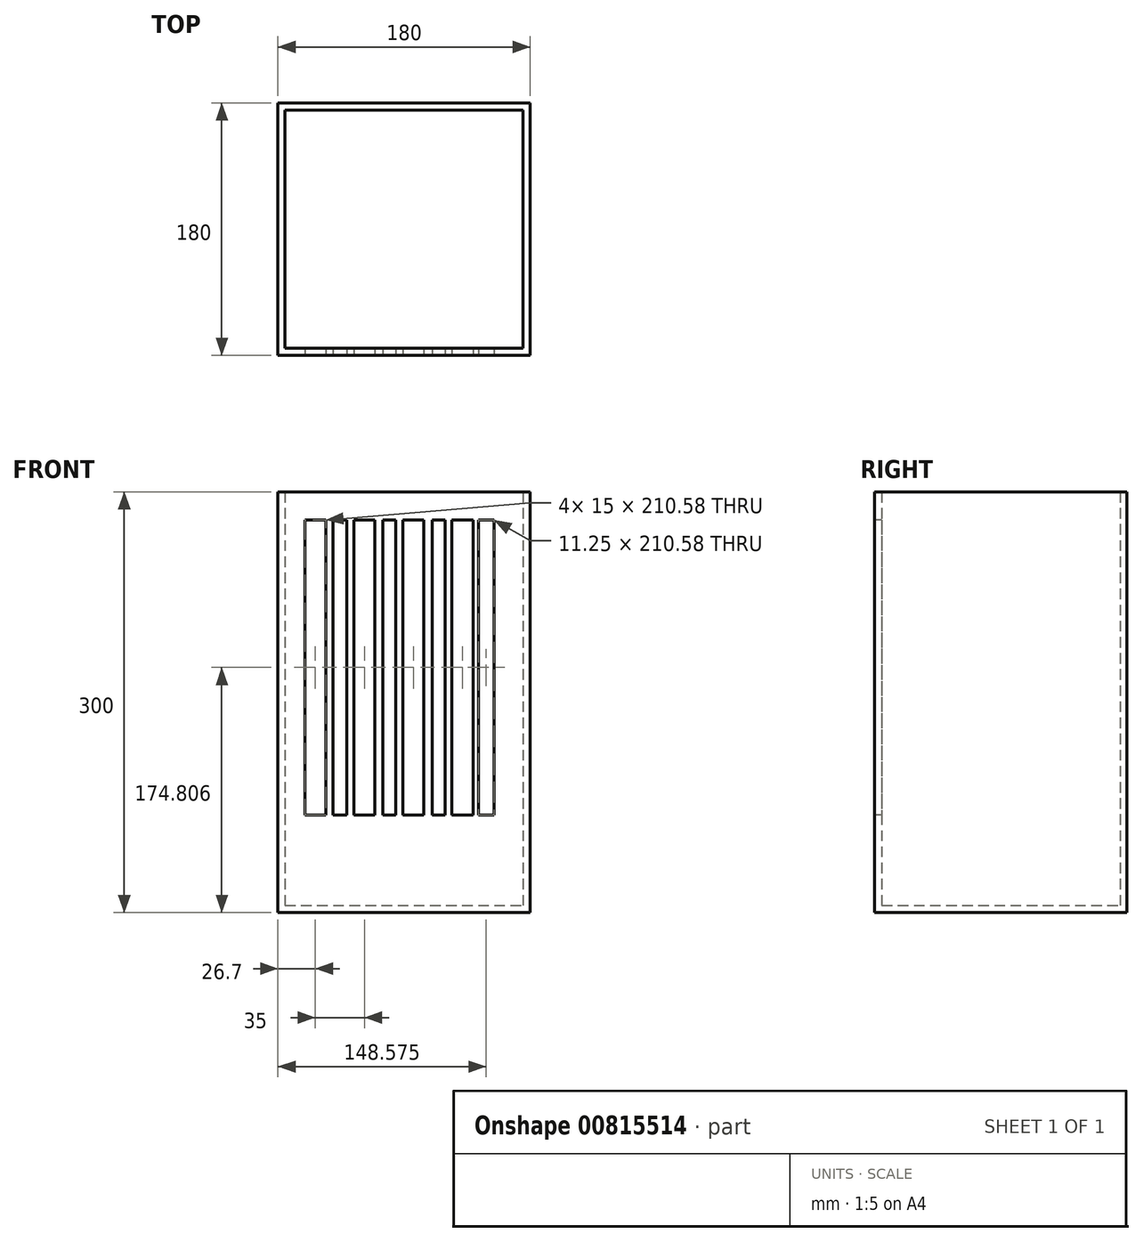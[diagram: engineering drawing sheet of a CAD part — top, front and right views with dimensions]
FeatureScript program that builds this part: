
annotation { "Feature Type Name" : "Feature", "Feature Type Description" : "" }
export const myFeature = defineFeature(function(context is Context, id is Id, definition is map)
    precondition{}
    {
        {
            var Q0;
            Q0=qCreatedBy(makeId("Front.planeOp"),FACE);
            var sketch = newSketch(context, id + "F0", { "sketchPlane" : qUnion([Q0])});
            skLineSegment(sketch, "E0.bottom", {"start": v(-142.95, 147.84) * mm, "end": v(37.05, 147.84) * mm});
            skLineSegment(sketch, "E0.top", {"start": v(-142.95, -152.16) * mm, "end": v(37.05, -152.16) * mm});
            skLineSegment(sketch, "E0.left", {"start": v(-142.95, 147.84) * mm, "end": v(-142.95, -152.16) * mm});
            skLineSegment(sketch, "E0.right", {"start": v(37.05, 147.84) * mm, "end": v(37.05, -152.16) * mm});
            skSolve(sketch);
        }
        {
            var Q0;
            Q0=makeQuery(id+"F0.imprint","IMPRINT",FACE,{"disambiguationData":[TD([[makeQuery(id+"F0.imprint","IMPRINT",EDGE,{"derivedFrom":sQuery(id+"F0.wireOp",EDGE,"E0.bottom")}),-1.0]])]});
            extrude(context, id + "F1", {"entities" : qUnion([Q0]), "depth" : 180 * mm, "offsetDistance" : 25 * mm});
        }
        {
            var Q0;
            Q0=makeQuery(id+"F1.opExtrude","SWEPT_FACE",FACE,{"disambiguationData":[OSD([sQuery(id+"F0.wireOp",EDGE,"E0.bottom")])]});
            shell(context, id + "F2", {"entities" : qUnion([Q0]), "thickness" : 5 * mm});
        }
        {
            var Q0;
            Q0=makeQuery(id+"F1.opExtrude","CAP_FACE",FACE,{"disambiguationData":[OSD([sQuery(id+"F0.wireOp",EDGE,"E0.bottom"),sQuery(id+"F0.wireOp",EDGE,"E0.top"),sQuery(id+"F0.wireOp",EDGE,"E0.left"),sQuery(id+"F0.wireOp",EDGE,"E0.right")])],"isStart":false});
            var sketch = newSketch(context, id + "F3", { "sketchPlane" : qUnion([Q0])});
            skLineSegment(sketch, "E1.bottom", {"start": v(-123.75, 127.94) * mm, "end": v(-108.75, 127.94) * mm});
            skLineSegment(sketch, "E1.top", {"start": v(-123.75, -82.65) * mm, "end": v(-108.75, -82.65) * mm});
            skLineSegment(sketch, "E1.left", {"start": v(-123.75, 127.94) * mm, "end": v(-123.75, -82.65) * mm});
            skLineSegment(sketch, "E1.right", {"start": v(-93.75, 127.94) * mm, "end": v(-93.75, -82.65) * mm});
            skLineSegment(sketch, "E2.bottom", {"start": v(-88.75, 127.94) * mm, "end": v(-73.75, 127.94) * mm});
            skLineSegment(sketch, "E2.top", {"start": v(-88.75, -82.65) * mm, "end": v(-73.75, -82.65) * mm});
            skLineSegment(sketch, "E2.left", {"start": v(-88.75, 127.94) * mm, "end": v(-88.75, -82.65) * mm});
            skLineSegment(sketch, "E2.right", {"start": v(-58.75, 127.94) * mm, "end": v(-58.75, -82.65) * mm});
            skLineSegment(sketch, "E3.bottom", {"start": v(-53.75, 127.94) * mm, "end": v(-38.75, 127.94) * mm});
            skLineSegment(sketch, "E3.top", {"start": v(-53.75, -82.65) * mm, "end": v(-38.75, -82.65) * mm});
            skLineSegment(sketch, "E3.left", {"start": v(-53.75, 127.94) * mm, "end": v(-53.75, -82.65) * mm});
            skLineSegment(sketch, "E3.right", {"start": v(-23.75, 127.94) * mm, "end": v(-23.75, -82.65) * mm});
            skLineSegment(sketch, "E4.bottom", {"start": v(-18.75, 127.94) * mm, "end": v(-3.75, 127.94) * mm});
            skLineSegment(sketch, "E4.top", {"start": v(-18.75, -82.65) * mm, "end": v(-3.75, -82.65) * mm});
            skLineSegment(sketch, "E4.left", {"start": v(-18.75, 127.94) * mm, "end": v(-18.75, -82.65) * mm});
            skLineSegment(sketch, "E4.right", {"start": v(11.25, 127.94) * mm, "end": v(11.25, -82.65) * mm});
            skLineSegment(sketch, "E5.left", {"start": v(-108.75, 127.94) * mm, "end": v(-108.75, -82.65) * mm});
            skLineSegment(sketch, "E5.right", {"start": v(-103.6, 127.94) * mm, "end": v(-103.6, -82.65) * mm});
            skLineSegment(sketch, "E6.left", {"start": v(-73.75, 127.94) * mm, "end": v(-73.75, -82.65) * mm});
            skLineSegment(sketch, "E6.right", {"start": v(-68.2, 127.94) * mm, "end": v(-68.2, -82.65) * mm});
            skLineSegment(sketch, "E7.left", {"start": v(-38.75, 127.94) * mm, "end": v(-38.75, -82.65) * mm});
            skLineSegment(sketch, "E7.right", {"start": v(-32.78, 127.94) * mm, "end": v(-32.78, -82.65) * mm});
            skPoint(sketch, "E8.oppositeSnap0", {"position": v(-3.75, -82.65) * mm});
            skLineSegment(sketch, "E8.left", {"start": v(-3.75, 127.94) * mm, "end": v(-3.75, -82.65) * mm});
            skLineSegment(sketch, "E8.right", {"start": v(0, 127.94) * mm, "end": v(0, -82.65) * mm});
            skLineSegment(sketch, "E9.trimOffspring", {"start": v(-103.6, -82.65) * mm, "end": v(-93.75, -82.65) * mm});
            skLineSegment(sketch, "E10.trimOffspring", {"start": v(-68.2, -82.65) * mm, "end": v(-58.75, -82.65) * mm});
            skLineSegment(sketch, "E11.trimOffspring", {"start": v(-32.78, -82.65) * mm, "end": v(-23.75, -82.65) * mm});
            skLineSegment(sketch, "E12.trimOffspring", {"start": v(0, -82.65) * mm, "end": v(11.25, -82.65) * mm});
            skLineSegment(sketch, "E13.trimOffspring", {"start": v(-103.6, 127.94) * mm, "end": v(-93.75, 127.94) * mm});
            skLineSegment(sketch, "E14.trimOffspring", {"start": v(-68.2, 127.94) * mm, "end": v(-58.75, 127.94) * mm});
            skLineSegment(sketch, "E15.trimOffspring", {"start": v(-32.78, 127.94) * mm, "end": v(-23.75, 127.94) * mm});
            skLineSegment(sketch, "E16.trimOffspring", {"start": v(0, 127.94) * mm, "end": v(11.25, 127.94) * mm});
            skSolve(sketch);
        }
        {
            var Q0;
            Q0 = qSketchRegion(id + "F3", true);
            extrude(context, id + "F4", {"entities" : qUnion([Q0]), "operationType" : NewBodyOperationType.REMOVE, "oppositeDirection" : true, "depth" : 25 * mm, "offsetDistance" : 25 * mm});
        }
    });
